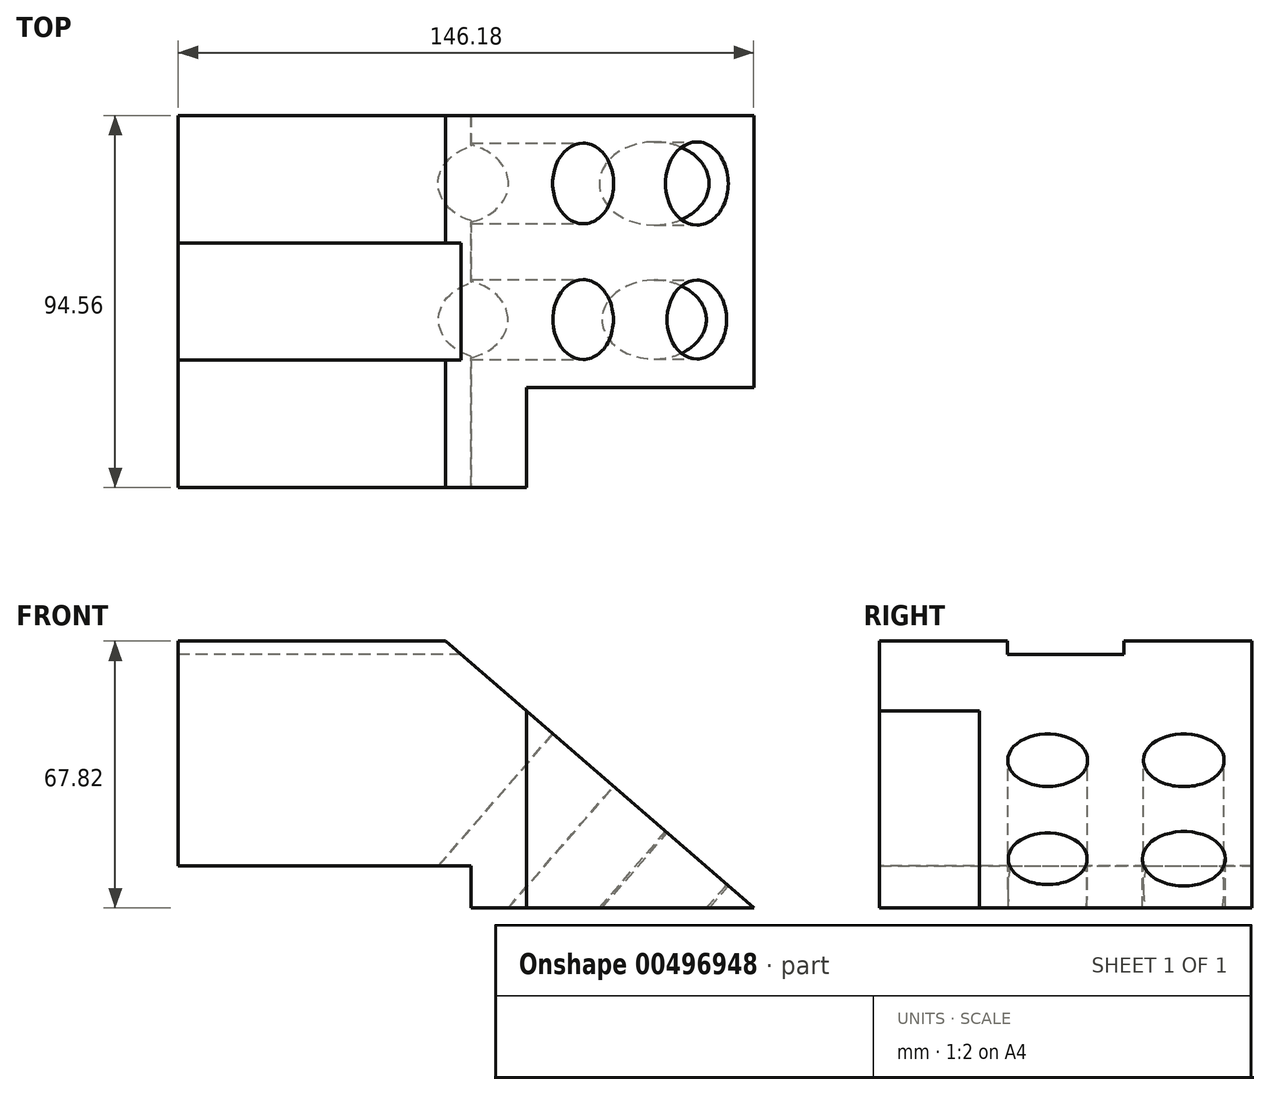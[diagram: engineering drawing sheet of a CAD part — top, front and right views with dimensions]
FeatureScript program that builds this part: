
annotation { "Feature Type Name" : "Feature", "Feature Type Description" : "" }
export const myFeature = defineFeature(function(context is Context, id is Id, definition is map)
    precondition{}
    {
        {
            var Q0;
            Q0=qCreatedBy(makeId("Top.planeOp"),FACE);
            var sketch = newSketch(context, id + "F0", { "sketchPlane" : qUnion([Q0])});
            skLineSegment(sketch, "E0.bottom", {"start": v(74.41, 47.28) * mm, "end": v(-74.41, 47.28) * mm});
            skLineSegment(sketch, "E0.top", {"start": v(74.41, -47.28) * mm, "end": v(-74.41, -47.28) * mm});
            skLineSegment(sketch, "E0.left", {"start": v(74.41, 47.28) * mm, "end": v(74.41, -47.28) * mm});
            skLineSegment(sketch, "E0.right", {"start": v(-74.41, 47.28) * mm, "end": v(-74.41, -47.28) * mm});
            skPoint(sketch, "E0.middle", {"position": v(0, 0) * mm});
            skSolve(sketch);
        }
        {
            var Q0;
            Q0 = qSketchRegion(id + "F0", true);
            extrude(context, id + "F1", {"entities" : qUnion([Q0]), "depth" : 67.82 * mm});
        }
        {
            var Q0;
            Q0=qCreatedBy(makeId("Front.planeOp"),FACE);
            var sketch = newSketch(context, id + "F2", { "sketchPlane" : qUnion([Q0])});
            skLineSegment(sketch, "E1", {"start": v(-11.2, 71.9) * mm, "end": v(83.4, -10.07) * mm});
            skLineSegment(sketch, "E2", {"start": v(83.4, -10.07) * mm, "end": v(83.4, 71.9) * mm});
            skLineSegment(sketch, "E3", {"start": v(83.4, 71.9) * mm, "end": v(-11.2, 71.9) * mm});
            skSolve(sketch);
        }
        {
            var Q0;
            Q0 = qSketchRegion(id + "F2", true);
            extrude(context, id + "F3", {"entities" : qUnion([Q0]), "operationType" : NewBodyOperationType.REMOVE, "depth" : 127 * mm, "symmetric" : true});
        }
        {
            var Q0;
            Q0=makeQuery(id+"F1.opExtrude","SWEPT_FACE",FACE,{"disambiguationData":[OSD([sQuery(id+"F0.wireOp",EDGE,"E0.top")])]});
            var sketch = newSketch(context, id + "F4", { "sketchPlane" : qUnion([Q0])});
            skLineSegment(sketch, "E4.bottom", {"start": v(-77.21, -4.76) * mm, "end": v(0, -4.76) * mm});
            skLineSegment(sketch, "E4.top", {"start": v(-77.21, 10.68) * mm, "end": v(0, 10.68) * mm});
            skLineSegment(sketch, "E4.left", {"start": v(-77.21, -4.76) * mm, "end": v(-77.21, 10.68) * mm});
            skLineSegment(sketch, "E4.right", {"start": v(0, -4.76) * mm, "end": v(0, 10.68) * mm});
            skSolve(sketch);
        }
        {
            var Q0;
            Q0 = qSketchRegion(id + "F4", true);
            extrude(context, id + "F5", {"entities" : qUnion([Q0]), "operationType" : NewBodyOperationType.REMOVE, "oppositeDirection" : true, "depth" : 100.33 * mm});
        }
        {
            var Q0;
            Q0=makeQuery(id+"F1.opExtrude","SWEPT_FACE",FACE,{"disambiguationData":[OSD([sQuery(id+"F0.wireOp",EDGE,"E0.top")])]});
            var sketch = newSketch(context, id + "F6", { "sketchPlane" : qUnion([Q0])});
            skLineSegment(sketch, "E5.bottom", {"start": v(13.99, -4.76) * mm, "end": v(73.3, -4.76) * mm});
            skLineSegment(sketch, "E5.top", {"start": v(13.99, 57.9) * mm, "end": v(73.3, 57.9) * mm});
            skLineSegment(sketch, "E5.left", {"start": v(13.99, -4.76) * mm, "end": v(13.99, 57.9) * mm});
            skLineSegment(sketch, "E5.right", {"start": v(73.3, -4.76) * mm, "end": v(73.3, 57.9) * mm});
            skSolve(sketch);
        }
        {
            var Q0;
            Q0 = qSketchRegion(id + "F6", true);
            extrude(context, id + "F7", {"entities" : qUnion([Q0]), "operationType" : NewBodyOperationType.REMOVE, "oppositeDirection" : true, "depth" : 25.4 * mm});
        }
        {
            var Q0;
            Q0=makeQuery(id+"F1.opExtrude","SWEPT_FACE",FACE,{"disambiguationData":[OSD([sQuery(id+"F0.wireOp",EDGE,"E0.right")])]});
            var sketch = newSketch(context, id + "F8", { "sketchPlane" : qUnion([Q0])});
            skLineSegment(sketch, "E6.bottom", {"start": v(14.83, 64.41) * mm, "end": v(-14.83, 64.41) * mm});
            skLineSegment(sketch, "E6.top", {"start": v(14.83, 71.22) * mm, "end": v(-14.83, 71.22) * mm});
            skLineSegment(sketch, "E6.left", {"start": v(14.83, 64.41) * mm, "end": v(14.83, 71.22) * mm});
            skLineSegment(sketch, "E6.right", {"start": v(-14.83, 64.41) * mm, "end": v(-14.83, 71.22) * mm});
            skPoint(sketch, "E6.middle", {"position": v(0, 67.82) * mm});
            skSolve(sketch);
        }
        {
            var Q0;
            Q0 = qSketchRegion(id + "F8", true);
            extrude(context, id + "F9", {"entities" : qUnion([Q0]), "operationType" : NewBodyOperationType.REMOVE, "oppositeDirection" : true, "depth" : 87.12 * mm});
        }
        {
            var Q0;
            Q0=makeQuery(id+"F3.boolean.opBoolean","COPY",FACE,{"derivedFrom":makeQuery(id+"F3.opExtrude","SWEPT_FACE",FACE,{"disambiguationData":[OSD([sQuery(id+"F2.wireOp",EDGE,"E1")])]})});
            var sketch = newSketch(context, id + "F10", { "sketchPlane" : qUnion([Q0])});
            skCircle(sketch, "E7", {"center": v(-3.1, -4.59) * mm, "radius": 10.15 * mm});
            skCircle(sketch, "E8", {"center": v(35.12, -4.59) * mm, "radius": 10.02 * mm});
            skCircle(sketch, "E9", {"center": v(35.12, 29.99) * mm, "radius": 10.56 * mm});
            skCircle(sketch, "E10", {"center": v(-3.1, 29.99) * mm, "radius": 10.24 * mm});
            skSolve(sketch);
        }
        {
            var Q0;
            Q0 = qSketchRegion(id + "F10", true);
            extrude(context, id + "F11", {"entities" : qUnion([Q0]), "operationType" : NewBodyOperationType.REMOVE, "oppositeDirection" : true, "depth" : 107.7 * mm});
        }
    });
